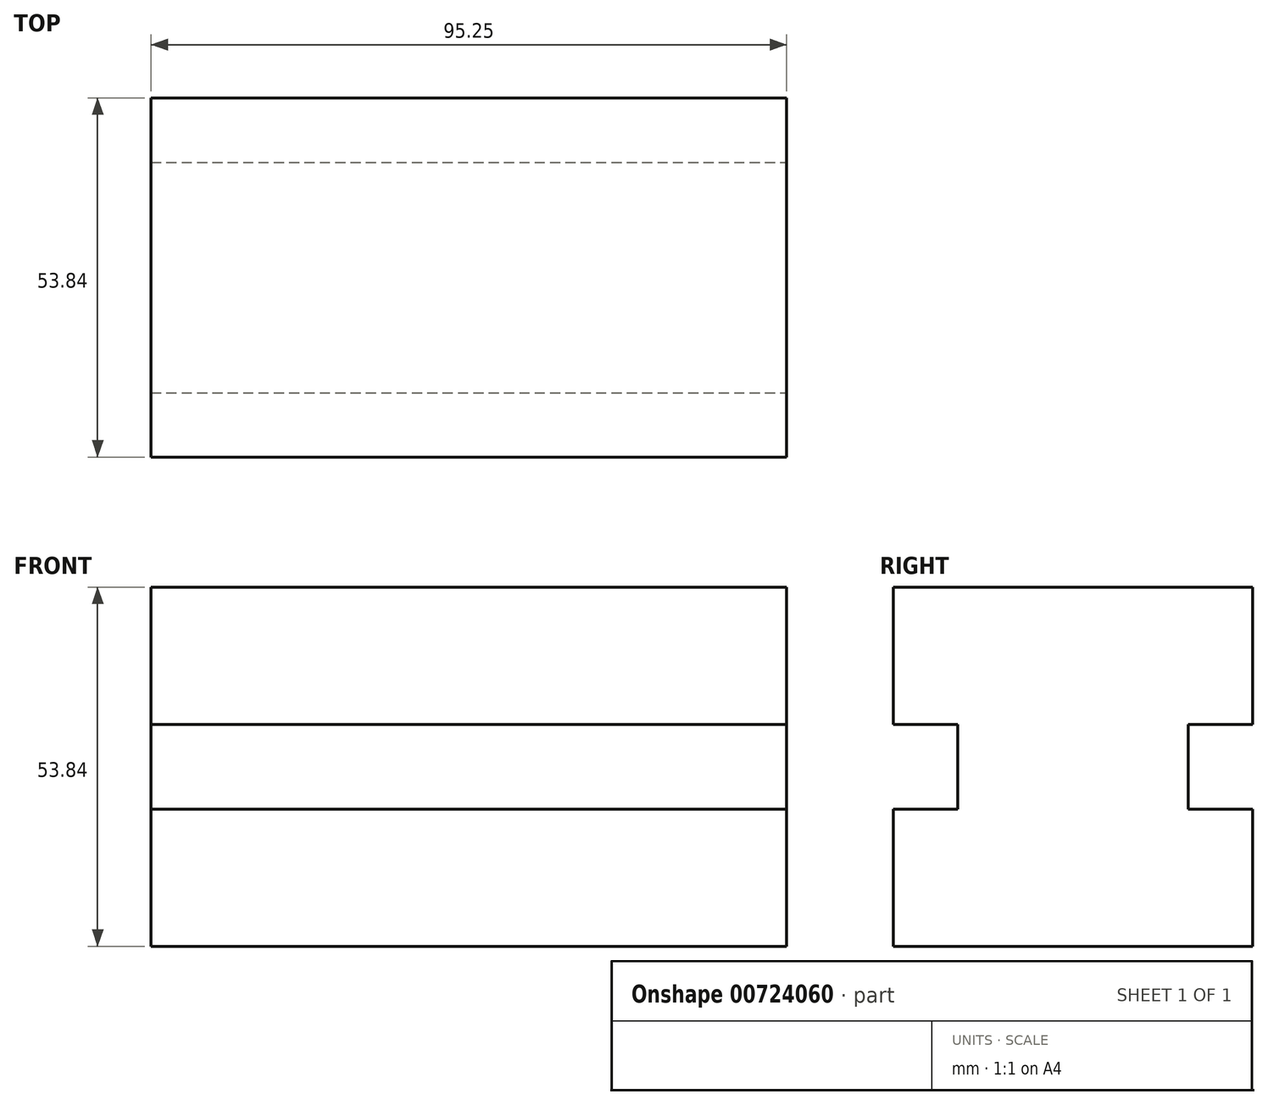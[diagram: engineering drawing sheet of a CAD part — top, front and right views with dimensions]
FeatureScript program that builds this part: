
annotation { "Feature Type Name" : "Feature", "Feature Type Description" : "" }
export const myFeature = defineFeature(function(context is Context, id is Id, definition is map)
    precondition{}
    {
        {
            var Q0;
            Q0=qCreatedBy(makeId("Right.planeOp"),FACE);
            var sketch = newSketch(context, id + "F0", { "sketchPlane" : qUnion([Q0])});
            skLineSegment(sketch, "E0.bottom", {"start": v(26.92, -26.92) * mm, "end": v(-26.92, -26.92) * mm});
            skLineSegment(sketch, "E0.top", {"start": v(26.92, 26.92) * mm, "end": v(-26.92, 26.92) * mm});
            skLineSegment(sketch, "E0.left", {"start": v(26.92, -26.92) * mm, "end": v(26.92, -6.35) * mm});
            skLineSegment(sketch, "E0.right", {"start": v(-26.92, -26.92) * mm, "end": v(-26.92, -6.35) * mm});
            skPoint(sketch, "E0.middle", {"position": v(0, 0) * mm});
            skLineSegment(sketch, "E1.bottom", {"start": v(-26.92, 6.35) * mm, "end": v(-17.27, 6.35) * mm});
            skLineSegment(sketch, "E1.top", {"start": v(-26.92, -6.35) * mm, "end": v(-17.27, -6.35) * mm});
            skLineSegment(sketch, "E1.right", {"start": v(-17.27, 6.35) * mm, "end": v(-17.27, -6.35) * mm});
            skLineSegment(sketch, "E2.trimOffspring", {"start": v(-26.92, 6.35) * mm, "end": v(-26.92, 26.92) * mm});
            skLineSegment(sketch, "E3", {"start": v(0, 36.49) * mm, "end": v(0, -26.92) * mm, "construction": true});
            skLineSegment(sketch, "E4.MirrorCS", {"start": v(26.92, 6.35) * mm, "end": v(17.27, 6.35) * mm});
            skLineSegment(sketch, "E5.MirrorCS", {"start": v(17.27, 6.35) * mm, "end": v(17.27, -6.35) * mm});
            skLineSegment(sketch, "E6.MirrorCS", {"start": v(26.92, -6.35) * mm, "end": v(17.27, -6.35) * mm});
            skLineSegment(sketch, "E7.trimOffspring", {"start": v(26.92, 6.35) * mm, "end": v(26.92, 26.92) * mm});
            skSolve(sketch);
        }
        {
            var Q0;
            Q0=makeQuery(id+"F0.imprint","IMPRINT",FACE,{"disambiguationData":[TD([[makeQuery(id+"F0.imprint","IMPRINT",EDGE,{"derivedFrom":sQuery(id+"F0.wireOp",EDGE,"E0.bottom")}),-1.0]])]});
            extrude(context, id + "F1", {"entities" : qUnion([Q0]), "oppositeDirection" : true, "depth" : 95.25 * mm, "offsetDistance" : 25.4 * mm});
        }
    });
